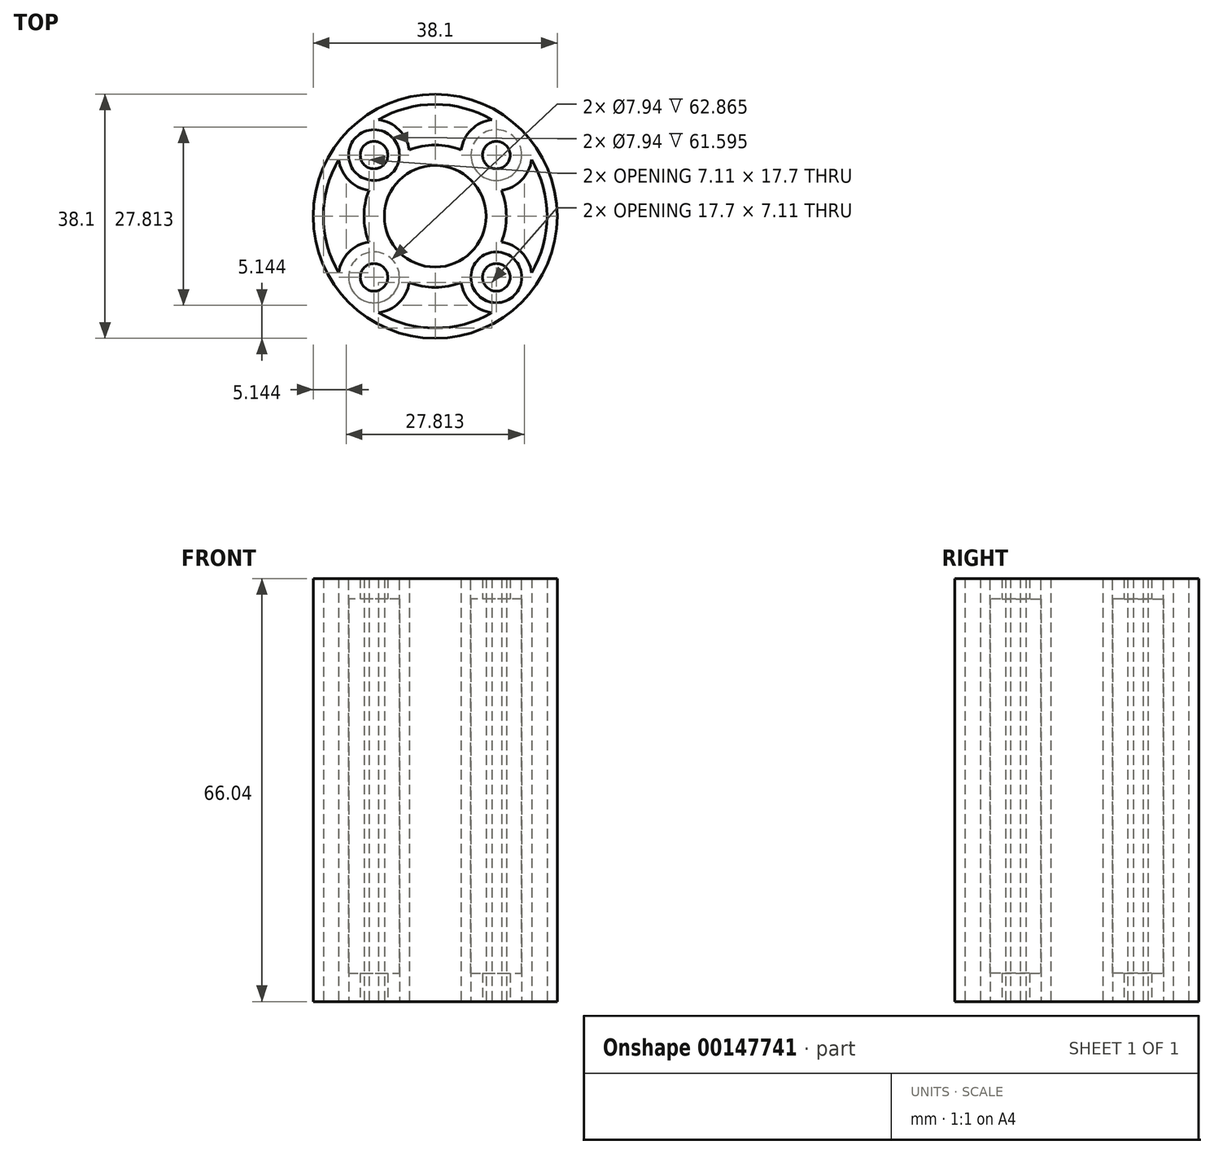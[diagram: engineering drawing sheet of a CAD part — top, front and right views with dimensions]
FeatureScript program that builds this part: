
annotation { "Feature Type Name" : "Feature", "Feature Type Description" : "" }
export const myFeature = defineFeature(function(context is Context, id is Id, definition is map)
    precondition{}
    {
        {
            var Q0;
            Q0=qCreatedBy(makeId("Top.planeOp"),FACE);
            var sketch = newSketch(context, id + "F0", { "sketchPlane" : qUnion([Q0])});
            skCircle(sketch, "E0", {"center": v(0, 0) * mm, "radius": 7.94 * mm});
            skLineSegment(sketch, "E1.bottom", {"start": v(9.54, 9.54) * mm, "end": v(-9.54, 9.54) * mm, "construction": true});
            skLineSegment(sketch, "E1.top", {"start": v(9.54, -9.54) * mm, "end": v(-9.54, -9.54) * mm, "construction": true});
            skLineSegment(sketch, "E1.left", {"start": v(9.54, 9.54) * mm, "end": v(9.54, -9.54) * mm, "construction": true});
            skLineSegment(sketch, "E1.right", {"start": v(-9.54, 9.54) * mm, "end": v(-9.54, -9.54) * mm, "construction": true});
            skCircle(sketch, "E2", {"center": v(-9.54, 9.54) * mm, "radius": 5.56 * mm, "construction": true});
            skLineSegment(sketch, "E3", {"start": v(0, 0) * mm, "end": v(0, 7.94) * mm});
            skCircle(sketch, "E4", {"center": v(-9.54, 9.54) * mm, "radius": 2.15 * mm});
            skCircle(sketch, "E5", {"center": v(-9.54, -9.54) * mm, "radius": 2.15 * mm});
            skCircle(sketch, "E6", {"center": v(9.54, -9.54) * mm, "radius": 2.15 * mm});
            skCircle(sketch, "E7", {"center": v(9.54, 9.54) * mm, "radius": 2.15 * mm});
            skCircle(sketch, "E8", {"center": v(0, 0) * mm, "radius": 19.05 * mm});
            skSolve(sketch);
        }
        {
            var Q0;
            Q0=qSketchRegion(id+"F0",true);
            extrude(context, id + "F1", {"entities" : qUnion([Q0]), "depth" : 66.04 * mm});
        }
        {
            var Q0;
            Q0=makeQuery(id+"F1.opExtrude","CAP_FACE",FACE,{"disambiguationData":[OSD([sQuery(id+"F0.wireOp",EDGE,"E0"),sQuery(id+"F0.wireOp",EDGE,"E4"),sQuery(id+"F0.wireOp",EDGE,"E5"),sQuery(id+"F0.wireOp",EDGE,"E6"),sQuery(id+"F0.wireOp",EDGE,"E7"),sQuery(id+"F0.wireOp",EDGE,"E8")])],"isStart":true});
            cPlane(context, id + "F2", {"entities" : qUnion([Q0]), "cplaneType" : CPlaneType.OFFSET, "offset" : 4.44 * mm, "oppositeDirection" : true, "width" : 152.4 * mm, "height" : 152.4 * mm});
        }
        {
            var Q0;
            Q0=makeQuery(id+"F1.opExtrude","CAP_FACE",FACE,{"disambiguationData":[OSD([sQuery(id+"F0.wireOp",EDGE,"E0"),sQuery(id+"F0.wireOp",EDGE,"E4"),sQuery(id+"F0.wireOp",EDGE,"E5"),sQuery(id+"F0.wireOp",EDGE,"E6"),sQuery(id+"F0.wireOp",EDGE,"E7"),sQuery(id+"F0.wireOp",EDGE,"E8")])],"isStart":false});
            cPlane(context, id + "F3", {"entities" : qUnion([Q0]), "cplaneType" : CPlaneType.OFFSET, "offset" : 3.17 * mm, "oppositeDirection" : true, "width" : 152.4 * mm, "height" : 152.4 * mm});
        }
        {
            var Q0;
            Q0=makeQuery(id+"F1.opExtrude","CAP_FACE",FACE,{"disambiguationData":[OSD([sQuery(id+"F0.wireOp",EDGE,"E0"),sQuery(id+"F0.wireOp",EDGE,"E4"),sQuery(id+"F0.wireOp",EDGE,"E5"),sQuery(id+"F0.wireOp",EDGE,"E6"),sQuery(id+"F0.wireOp",EDGE,"E7"),sQuery(id+"F0.wireOp",EDGE,"E8")])],"isStart":true});
            var sketch = newSketch(context, id + "F4", { "sketchPlane" : qUnion([Q0])});
            skCircle(sketch, "E9", {"center": v(9.54, -9.54) * mm, "radius": 3.97 * mm});
            skCircle(sketch, "E10", {"center": v(-9.54, 9.54) * mm, "radius": 3.97 * mm});
            skSolve(sketch);
        }
        {
            var Q0;
            Q0=qSketchRegion(id+"F4",true);
            var Q1;
            Q1=qCreatedBy(id+"F3.planeOp",FACE);
            extrude(context, id + "F5", {"entities" : qUnion([Q0]), "operationType" : NewBodyOperationType.REMOVE, "endBound" : BoundingType.UP_TO_SURFACE, "oppositeDirection" : true, "endBoundEntityFace" : qUnion([Q1]), "depth" : 25.4 * mm});
        }
        {
            var Q0;
            Q0=makeQuery(id+"F1.opExtrude","CAP_FACE",FACE,{"disambiguationData":[OSD([sQuery(id+"F0.wireOp",EDGE,"E0"),sQuery(id+"F0.wireOp",EDGE,"E4"),sQuery(id+"F0.wireOp",EDGE,"E5"),sQuery(id+"F0.wireOp",EDGE,"E6"),sQuery(id+"F0.wireOp",EDGE,"E7"),sQuery(id+"F0.wireOp",EDGE,"E8")])],"isStart":false});
            var sketch = newSketch(context, id + "F6", { "sketchPlane" : qUnion([Q0])});
            skCircle(sketch, "E11", {"center": v(-9.54, 9.54) * mm, "radius": 3.97 * mm});
            skCircle(sketch, "E12", {"center": v(9.54, -9.54) * mm, "radius": 3.97 * mm});
            skSolve(sketch);
        }
        {
            var Q0;
            Q0=qSketchRegion(id+"F6",true);
            var Q1;
            Q1=qCreatedBy(id+"F2.planeOp",FACE);
            extrude(context, id + "F7", {"entities" : qUnion([Q0]), "operationType" : NewBodyOperationType.REMOVE, "endBound" : BoundingType.UP_TO_SURFACE, "oppositeDirection" : true, "endBoundEntityFace" : qUnion([Q1]), "depth" : 25.4 * mm});
        }
        {
            var Q0;
            Q0=makeQuery(id+"F1.opExtrude","CAP_FACE",FACE,{"disambiguationData":[OSD([sQuery(id+"F0.wireOp",EDGE,"E0"),sQuery(id+"F0.wireOp",EDGE,"E4"),sQuery(id+"F0.wireOp",EDGE,"E5"),sQuery(id+"F0.wireOp",EDGE,"E6"),sQuery(id+"F0.wireOp",EDGE,"E7"),sQuery(id+"F0.wireOp",EDGE,"E8")])],"isStart":true});
            var sketch = newSketch(context, id + "F8", { "sketchPlane" : qUnion([Q0])});
            skArc(sketch, "E13", {"start": v(4.04, -10.35) * mm, "mid": v(5.65, -13.51) * mm, "end": v(8.85, -15.05) * mm});
            skArc(sketch, "E14", {"start": v(-8.85, -15.05) * mm, "mid": v(0, -17.46) * mm, "end": v(8.85, -15.05) * mm});
            skArc(sketch, "E15", {"start": v(-4.04, -10.35) * mm, "mid": v(0, -11.11) * mm, "end": v(4.04, -10.35) * mm});
            skArc(sketch, "E16", {"start": v(-8.85, -15.05) * mm, "mid": v(-5.65, -13.51) * mm, "end": v(-4.04, -10.35) * mm});
            skSolve(sketch);
        }
        {
            var Q0;
            Q0=qSketchRegion(id+"F8",true);
            var Q1;
            Q1=makeQuery(id+"F1.opExtrude","CAP_FACE",FACE,{"disambiguationData":[OSD([sQuery(id+"F0.wireOp",EDGE,"E0"),sQuery(id+"F0.wireOp",EDGE,"E4"),sQuery(id+"F0.wireOp",EDGE,"E5"),sQuery(id+"F0.wireOp",EDGE,"E6"),sQuery(id+"F0.wireOp",EDGE,"E7"),sQuery(id+"F0.wireOp",EDGE,"E8")])],"isStart":false});
            extrude(context, id + "F9", {"entities" : qUnion([Q0]), "operationType" : NewBodyOperationType.REMOVE, "endBound" : BoundingType.UP_TO_SURFACE, "oppositeDirection" : true, "endBoundEntityFace" : qUnion([Q1]), "depth" : 25.4 * mm});
        }
        {
            var Q0;
            Q0=makeQuery(id+"F9.boolean.opBoolean","COPY",FACE,{"derivedFrom":makeQuery(id+"F9.opExtrude","SWEPT_FACE",FACE,{"disambiguationData":[OSD([sQuery(id+"F8.wireOp",EDGE,"E14")])]})});
            var Q1;
            Q1=makeQuery(id+"F9.boolean.opBoolean","COPY",FACE,{"derivedFrom":makeQuery(id+"F9.opExtrude","SWEPT_FACE",FACE,{"disambiguationData":[OSD([sQuery(id+"F8.wireOp",EDGE,"E16")])]})});
            var Q2;
            Q2=makeQuery(id+"F9.boolean.opBoolean","COPY",FACE,{"derivedFrom":makeQuery(id+"F9.opExtrude","SWEPT_FACE",FACE,{"disambiguationData":[OSD([sQuery(id+"F8.wireOp",EDGE,"E15")])]})});
            var Q3;
            Q3=makeQuery(id+"F9.boolean.opBoolean","COPY",FACE,{"derivedFrom":makeQuery(id+"F9.opExtrude","SWEPT_FACE",FACE,{"disambiguationData":[OSD([sQuery(id+"F8.wireOp",EDGE,"E13")])]})});
            var Q4;
            Q4=makeQuery(id+"F1.opExtrude","SWEPT_FACE",FACE,{"disambiguationData":[OSD([sQuery(id+"F0.wireOp",EDGE,"E8")])]});
            circularPattern(context, id + "F10", {"patternType" : PatternType.FACE, "faces" : qUnion([Q0, Q1, Q2, Q3]), "axis" : qUnion([Q4]), "angle" : 90 * degree, "instanceCount" : 4});
        }
    });
